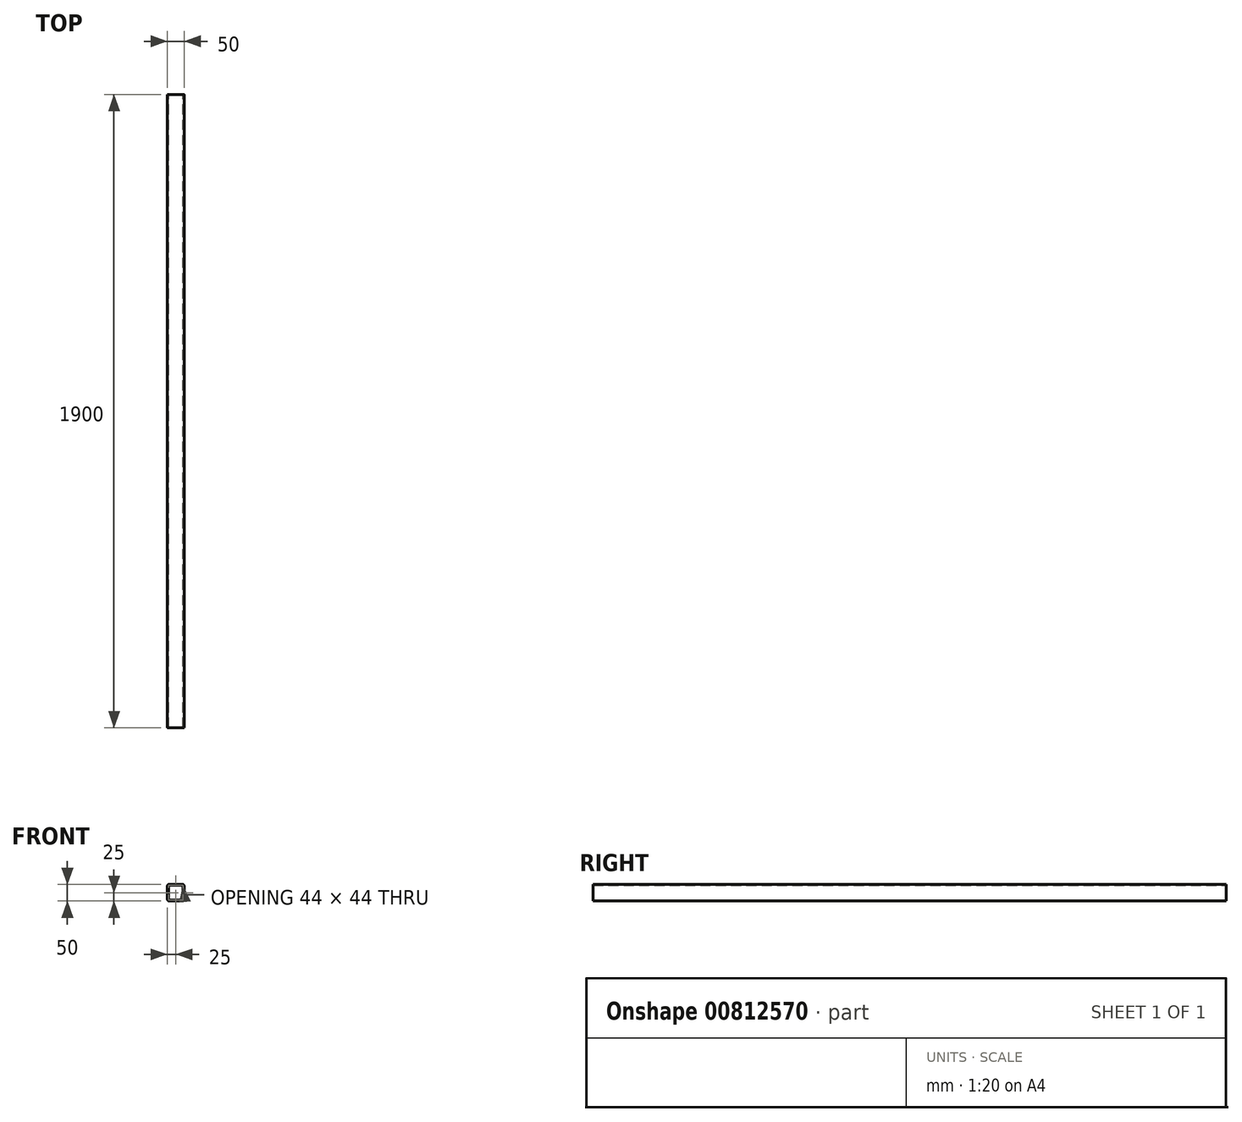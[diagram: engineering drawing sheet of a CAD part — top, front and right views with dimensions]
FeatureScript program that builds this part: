
annotation { "Feature Type Name" : "Feature", "Feature Type Description" : "" }
export const myFeature = defineFeature(function(context is Context, id is Id, definition is map)
    precondition{}
    {
        {
            var Q0;
            Q0=qCreatedBy(makeId("Front.planeOp"),FACE);
            var sketch = newSketch(context, id + "F0", { "sketchPlane" : qUnion([Q0])});
            skLineSegment(sketch, "E0.bottom", {"start": v(50, 50) * mm, "end": v(0, 50) * mm});
            skLineSegment(sketch, "E0.top", {"start": v(50, 0) * mm, "end": v(0, 0) * mm});
            skLineSegment(sketch, "E0.left", {"start": v(50, 50) * mm, "end": v(50, 0) * mm});
            skLineSegment(sketch, "E0.right", {"start": v(0, 50) * mm, "end": v(0, 0) * mm});
            skLineSegment(sketch, "E1.0", {"start": v(47, 3) * mm, "end": v(3, 3) * mm});
            skLineSegment(sketch, "E1.1", {"start": v(47, 47) * mm, "end": v(47, 3) * mm});
            skLineSegment(sketch, "E1.2", {"start": v(47, 47) * mm, "end": v(3, 47) * mm});
            skLineSegment(sketch, "E1.3", {"start": v(3, 47) * mm, "end": v(3, 3) * mm});
            skSolve(sketch);
        }
        {
            var Q0;
            Q0 = qSketchRegion(id + "F0", true);
            extrude(context, id + "F1", {"entities" : qUnion([Q0]), "depth" : 1900 * mm, "offsetDistance" : 25 * mm});
        }
        {
            var Q0;
            Q0 = qSketchRegion(id + "F0", true);
            extrude(context, id + "F2", {"entities" : qUnion([Q0]), "operationType" : NewBodyOperationType.ADD, "depth" : 100 * mm, "offsetDistance" : 25 * mm});
        }
        {
            var Q0;
            Q0=makeQuery(id+"F1.opExtrude","SWEPT_EDGE",EDGE,{"disambiguationData":[OSD([sQuery(id+"F0.wireOp",EDGE,"E0.bottom"),sQuery(id+"F0.wireOp",EDGE,"E0.left")])]});
            var Q1;
            Q1=makeQuery(id+"F1.opExtrude","SWEPT_EDGE",EDGE,{"disambiguationData":[OSD([sQuery(id+"F0.wireOp",EDGE,"E0.top"),sQuery(id+"F0.wireOp",EDGE,"E0.left")])]});
            var Q2;
            Q2=makeQuery(id+"F1.opExtrude","SWEPT_EDGE",EDGE,{"disambiguationData":[OSD([sQuery(id+"F0.wireOp",EDGE,"E0.top"),sQuery(id+"F0.wireOp",EDGE,"E0.right")])]});
            var Q3;
            Q3=makeQuery(id+"F1.opExtrude","SWEPT_EDGE",EDGE,{"disambiguationData":[OSD([sQuery(id+"F0.wireOp",EDGE,"E0.bottom"),sQuery(id+"F0.wireOp",EDGE,"E0.right")])]});
            fillet(context, id + "F3", {"entities" : qUnion([Q0, Q1, Q2, Q3]), "radius" : 5 * mm, "tangentPropagation" : true, "allowEdgeOverflow" : false});
        }
        {
            var Q0;
            Q0=makeQuery(id+"F1.opExtrude","SWEPT_EDGE",EDGE,{"disambiguationData":[OSD([sQuery(id+"F0.wireOp",EDGE,"E1.1"),sQuery(id+"F0.wireOp",EDGE,"E1.2")])]});
            var Q1;
            Q1=makeQuery(id+"F1.opExtrude","SWEPT_EDGE",EDGE,{"disambiguationData":[OSD([sQuery(id+"F0.wireOp",EDGE,"E1.0"),sQuery(id+"F0.wireOp",EDGE,"E1.3")])]});
            var Q2;
            Q2=makeQuery(id+"F1.opExtrude","SWEPT_EDGE",EDGE,{"disambiguationData":[OSD([sQuery(id+"F0.wireOp",EDGE,"E1.2"),sQuery(id+"F0.wireOp",EDGE,"E1.3")])]});
            var Q3;
            Q3=makeQuery(id+"F1.opExtrude","SWEPT_EDGE",EDGE,{"disambiguationData":[OSD([sQuery(id+"F0.wireOp",EDGE,"E1.0"),sQuery(id+"F0.wireOp",EDGE,"E1.1")])]});
            fillet(context, id + "F4", {"entities" : qUnion([Q0, Q1, Q2, Q3]), "radius" : 3 * mm, "tangentPropagation" : true, "allowEdgeOverflow" : false});
        }
    });
